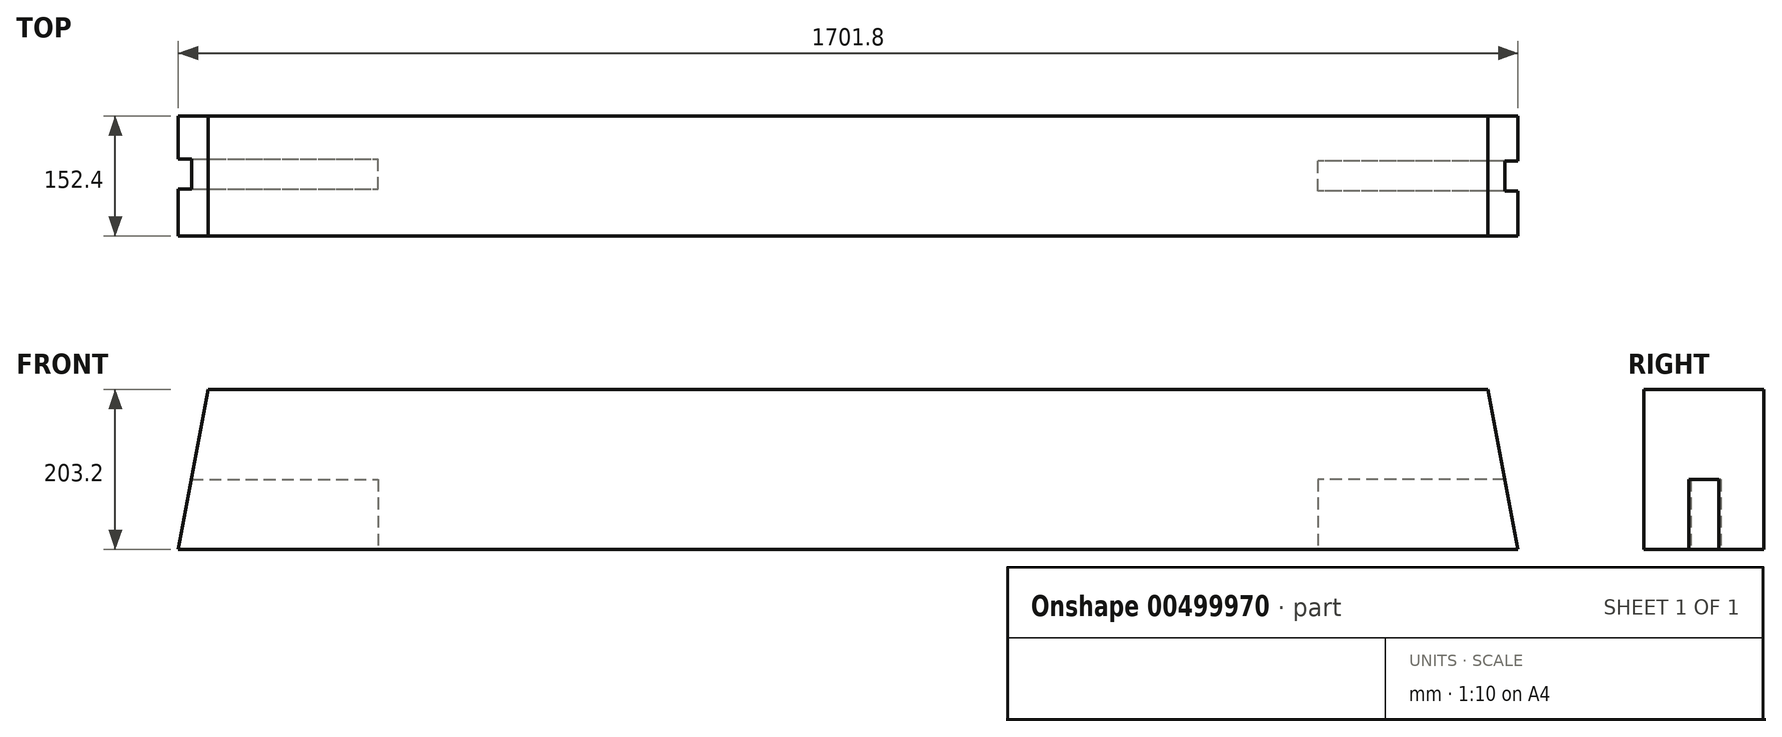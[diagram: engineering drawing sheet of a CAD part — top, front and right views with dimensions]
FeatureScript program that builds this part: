
annotation { "Feature Type Name" : "Feature", "Feature Type Description" : "" }
export const myFeature = defineFeature(function(context is Context, id is Id, definition is map)
    precondition{}
    {
        {
            var Q0;
            Q0=qCreatedBy(makeId("Front.planeOp"),FACE);
            var sketch = newSketch(context, id + "F0", { "sketchPlane" : qUnion([Q0])});
            skLineSegment(sketch, "E0.bottom", {"start": v(-850.9, 101.6) * mm, "end": v(850.9, 101.6) * mm});
            skLineSegment(sketch, "E0.top", {"start": v(-850.9, -101.6) * mm, "end": v(850.9, -101.6) * mm});
            skLineSegment(sketch, "E0.left", {"start": v(-850.9, 101.6) * mm, "end": v(-850.9, -101.6) * mm});
            skLineSegment(sketch, "E0.right", {"start": v(850.9, 101.6) * mm, "end": v(850.9, -101.6) * mm});
            skPoint(sketch, "E0.middle", {"position": v(0, 0) * mm});
            skLineSegment(sketch, "E1", {"start": v(-850.9, -101.6) * mm, "end": v(-812.8, 101.6) * mm});
            skLineSegment(sketch, "E2", {"start": v(850.9, -101.6) * mm, "end": v(812.8, 101.6) * mm});
            skSolve(sketch);
        }
        {
            var Q0;
            Q0=makeQuery(id+"F0.imprint","IMPRINT",FACE,{"disambiguationData":[TD([[makeQuery(id+"F0.imprint","IMPRINT",EDGE,{"derivedFrom":sQuery(id+"F0.wireOp",EDGE,"E0.top")}),1.0]])]});
            extrude(context, id + "F1", {"entities" : qUnion([Q0]), "depth" : 152.4 * mm, "offsetDistance" : 25.4 * mm});
        }
        {
            var Q0;
            Q0=makeQuery(id+"F1.opExtrude","SWEPT_FACE",FACE,{"disambiguationData":[OSD([sQuery(id+"F0.wireOp",EDGE,"E0.top")])]});
            var sketch = newSketch(context, id + "F2", { "sketchPlane" : qUnion([Q0])});
            skLineSegment(sketch, "E3.bottom", {"start": v(-850.9, 92.71) * mm, "end": v(-596.9, 92.71) * mm});
            skLineSegment(sketch, "E3.top", {"start": v(-850.9, 54.61) * mm, "end": v(-596.9, 54.61) * mm});
            skLineSegment(sketch, "E3.left", {"start": v(-850.9, 92.71) * mm, "end": v(-850.9, 54.61) * mm});
            skLineSegment(sketch, "E3.right", {"start": v(-596.9, 92.71) * mm, "end": v(-596.9, 54.61) * mm});
            skLineSegment(sketch, "E4.bottom", {"start": v(850.9, 95.25) * mm, "end": v(596.9, 95.25) * mm});
            skLineSegment(sketch, "E4.top", {"start": v(850.9, 57.15) * mm, "end": v(596.9, 57.15) * mm});
            skLineSegment(sketch, "E4.left", {"start": v(850.9, 95.25) * mm, "end": v(850.9, 57.15) * mm});
            skLineSegment(sketch, "E4.right", {"start": v(596.9, 95.25) * mm, "end": v(596.9, 57.15) * mm});
            skSolve(sketch);
        }
        {
            var Q0;
            Q0=qSketchRegion(id+"F2",true);
            extrude(context, id + "F3", {"entities" : qUnion([Q0]), "operationType" : NewBodyOperationType.REMOVE, "oppositeDirection" : true, "depth" : 88.9 * mm, "offsetDistance" : 25.4 * mm});
        }
    });
